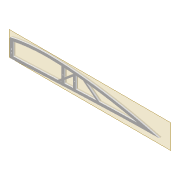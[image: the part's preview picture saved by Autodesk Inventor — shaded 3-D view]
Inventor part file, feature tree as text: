
AUTODESK INVENTOR PART (.ipt)
format: ipt  version: 2022 (Build 260153000, 153)  size: 344,576 bytes
history: native  units: mm
features: extrude x6, sketch x6, projected_geometry x5, shell x1, fillet x1, plane x1
ambient origin geometry x8: Origin, YZ Plane, XZ Plane, XY Plane, X Axis, Y Axis, Z Axis, Center Point
bodies: Solid1 (feature_tree)
feature tree (20):
  extrude  "Extrusion1"  Depth=5.0mm
  shell  "Shell1"  Thickness=6.0mm
  extrude  "Extrusion2"  Depth=2.0mm
  extrude  "Extrusion3"  Depth=5.9mm
  extrude  "Extrusion4"  Depth=10.0mm TaperAngle=0.0deg
  fillet  "Fillet1"  Radius=40.0mm
  extrude  "Extrusion5"  Depth=10.0mm
  plane  "Work Plane2"
  extrude  "Extrusion7"  Depth=5.0mm
  sketch  "Sketch3"  dims[d0=4.0mm d1=0.0mm d2=5.0mm d3=6.0mm]
  sketch  "Sketch7"  dims[d5=4.0mm d6=0.0mm d7=2.0mm]
  projected_geometry  "Projected Loop3"
  sketch  "Sketch8"  dims[d8=2.0mm d9=5.9mm]
  sketch  "Sketch9"  dims[d12=4.0mm d13=10.0mm d14=0.0mm d15=40.0mm]
  sketch  "Sketch10"  dims[d16=10.0mm d17=0.0mm d18=3.0mm]
  projected_geometry  "Projected Loop4"
  sketch  "Sketch14"  dims[d19=3.0mm d20=3.0mm d22=4.0mm d23=0.0mm d24=2.0mm d26=2.0mm d29=4.0mm d30=0.0mm d31=2.0mm d32=5.0mm d33=130.0mm d34=1.6mm d35=2.5mm d36=12.0mm d37=5.0mm d38=1.6mm d39=150.0mm d40=2.5mm]
  projected_geometry  "Projected Loop7"
  projected_geometry  "Projected Loop9"
  projected_geometry  "Projected Loop10"
